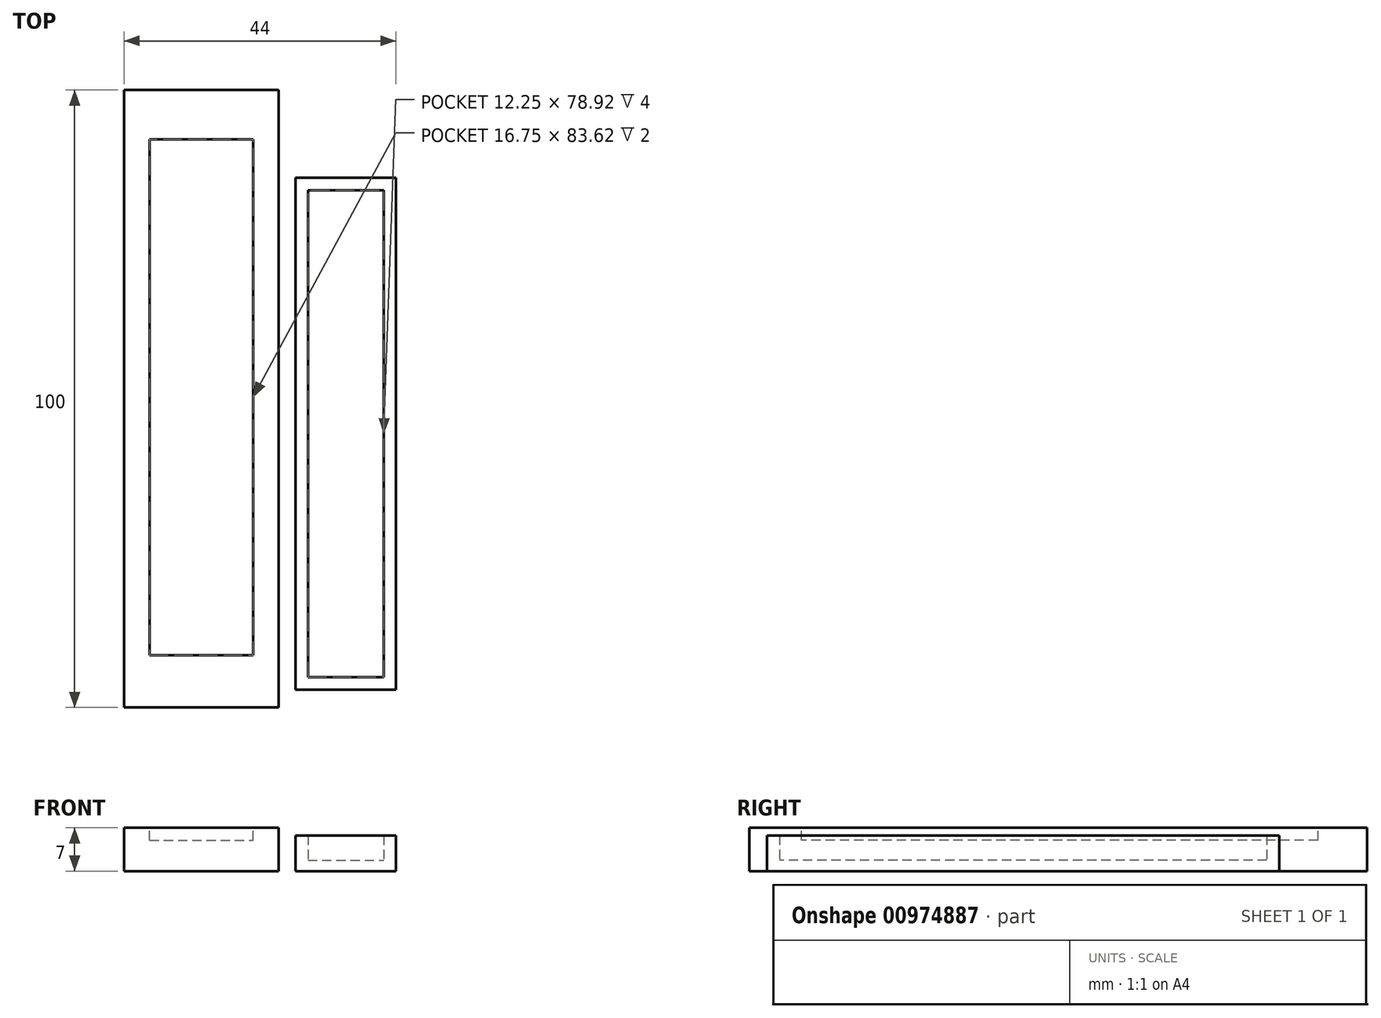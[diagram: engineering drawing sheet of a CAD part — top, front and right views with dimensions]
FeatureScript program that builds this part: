
annotation { "Feature Type Name" : "Feature", "Feature Type Description" : "" }
export const myFeature = defineFeature(function(context is Context, id is Id, definition is map)
    precondition{}
    {
        {
            var Q0;
            Q0=qCreatedBy(makeId("Top.planeOp"),FACE);
            var sketch = newSketch(context, id + "F0", { "sketchPlane" : qUnion([Q0])});
            skLineSegment(sketch, "E0.bottom", {"start": v(0, 0) * mm, "end": v(25, 0) * mm});
            skLineSegment(sketch, "E0.top", {"start": v(0, 100) * mm, "end": v(25, 100) * mm});
            skLineSegment(sketch, "E0.left", {"start": v(0, 0) * mm, "end": v(0, 100) * mm});
            skLineSegment(sketch, "E0.right", {"start": v(25, 0) * mm, "end": v(25, 100) * mm});
            skSolve(sketch);
        }
        {
            var Q0;
            Q0=qSketchRegion(id+"F0",true);
            extrude(context, id + "F1", {"entities" : qUnion([Q0]), "depth" : 7 * mm, "offsetDistance" : 25 * mm});
        }
        {
            var Q0;
            Q0=makeQuery(id+"F1.opExtrude","CAP_FACE",FACE,{"disambiguationData":[OSD([sQuery(id+"F0.wireOp",EDGE,"E0.bottom"),sQuery(id+"F0.wireOp",EDGE,"E0.top"),sQuery(id+"F0.wireOp",EDGE,"E0.left"),sQuery(id+"F0.wireOp",EDGE,"E0.right"),sQuery(id+"F0.wireOp",EDGE,"tL0FAtRF-50eW-EPkH-YYZn-dPz8Ajvxfmio.bottom"),sQuery(id+"F0.wireOp",EDGE,"tL0FAtRF-50eW-EPkH-YYZn-dPz8Ajvxfmio.top"),sQuery(id+"F0.wireOp",EDGE,"tL0FAtRF-50eW-EPkH-YYZn-dPz8Ajvxfmio.left"),sQuery(id+"F0.wireOp",EDGE,"tL0FAtRF-50eW-EPkH-YYZn-dPz8Ajvxfmio.right")])],"isStart":false});
            var sketch = newSketch(context, id + "F2", { "sketchPlane" : qUnion([Q0])});
            skLineSegment(sketch, "E1.bottom", {"start": v(4.12, 92.06) * mm, "end": v(20.87, 92.06) * mm});
            skLineSegment(sketch, "E1.top", {"start": v(4.12, 8.44) * mm, "end": v(20.87, 8.44) * mm});
            skLineSegment(sketch, "E1.left", {"start": v(4.12, 92.06) * mm, "end": v(4.12, 8.44) * mm});
            skLineSegment(sketch, "E1.right", {"start": v(20.87, 92.06) * mm, "end": v(20.87, 8.44) * mm});
            skSolve(sketch);
        }
        {
            var Q0;
            Q0=qSketchRegion(id+"F2",true);
            extrude(context, id + "F3", {"entities" : qUnion([Q0]), "operationType" : NewBodyOperationType.REMOVE, "oppositeDirection" : true, "depth" : 2 * mm, "offsetDistance" : 25 * mm});
        }
        {
            var Q0;
            Q0=qCreatedBy(makeId("Top.planeOp"),FACE);
            var sketch = newSketch(context, id + "F4", { "sketchPlane" : qUnion([Q0])});
            skLineSegment(sketch, "E2.bottom", {"start": v(27.75, 85.8) * mm, "end": v(44, 85.8) * mm});
            skLineSegment(sketch, "E2.top", {"start": v(27.75, 2.88) * mm, "end": v(44, 2.88) * mm});
            skLineSegment(sketch, "E2.left", {"start": v(27.75, 85.8) * mm, "end": v(27.75, 2.88) * mm});
            skLineSegment(sketch, "E2.right", {"start": v(44, 85.8) * mm, "end": v(44, 2.88) * mm});
            skSolve(sketch);
        }
        {
            var Q0;
            Q0=qSketchRegion(id+"F4",true);
            extrude(context, id + "F5", {"entities" : qUnion([Q0]), "depth" : 1.75 * mm, "offsetDistance" : 25 * mm});
        }
        {
            var Q0;
            Q0=makeQuery(id+"F5.opExtrude","CAP_FACE",FACE,{"disambiguationData":[OSD([sQuery(id+"F4.wireOp",EDGE,"E2.bottom"),sQuery(id+"F4.wireOp",EDGE,"E2.top"),sQuery(id+"F4.wireOp",EDGE,"E2.left"),sQuery(id+"F4.wireOp",EDGE,"E2.right")])],"isStart":false});
            var sketch = newSketch(context, id + "F6", { "sketchPlane" : qUnion([Q0])});
            skLineSegment(sketch, "E3.bottom", {"start": v(27.75, 85.8) * mm, "end": v(44, 85.8) * mm});
            skLineSegment(sketch, "E3.top", {"start": v(27.75, 2.88) * mm, "end": v(44, 2.88) * mm});
            skLineSegment(sketch, "E3.left", {"start": v(27.75, 85.8) * mm, "end": v(27.75, 2.88) * mm});
            skLineSegment(sketch, "E3.right", {"start": v(44, 85.8) * mm, "end": v(44, 2.88) * mm});
            skLineSegment(sketch, "E4.bottom", {"start": v(29.75, 83.8) * mm, "end": v(42, 83.8) * mm});
            skLineSegment(sketch, "E4.top", {"start": v(29.75, 4.88) * mm, "end": v(42, 4.88) * mm});
            skLineSegment(sketch, "E4.left", {"start": v(29.75, 83.8) * mm, "end": v(29.75, 4.88) * mm});
            skLineSegment(sketch, "E4.right", {"start": v(42, 83.8) * mm, "end": v(42, 4.88) * mm});
            skSolve(sketch);
        }
        {
            var Q0;
            Q0 = qSketchRegion(id + "F6", true);
            extrude(context, id + "F7", {"entities" : qUnion([Q0]), "operationType" : NewBodyOperationType.ADD, "depth" : 4 * mm, "offsetDistance" : 25 * mm});
        }
    });
